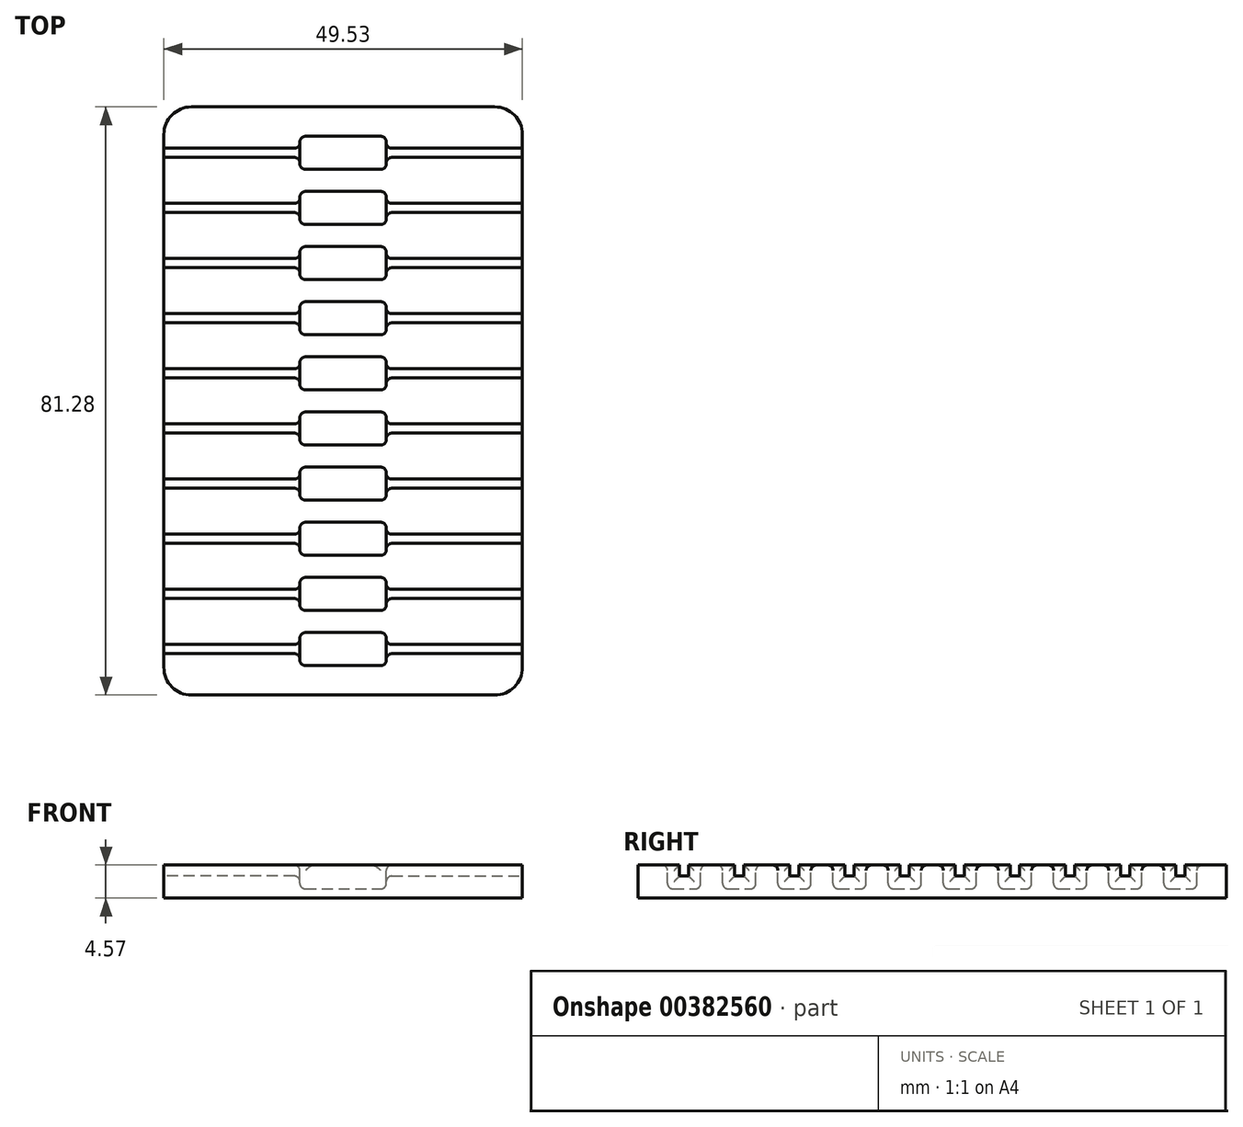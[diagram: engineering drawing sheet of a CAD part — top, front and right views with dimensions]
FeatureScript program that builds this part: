
annotation { "Feature Type Name" : "Feature", "Feature Type Description" : "" }
export const myFeature = defineFeature(function(context is Context, id is Id, definition is map)
    precondition{}
    {
        {
            var Q0;
            Q0=qCreatedBy(makeId("Top.planeOp"),FACE);
            var sketch = newSketch(context, id + "F0", { "sketchPlane" : qUnion([Q0])});
            skLineSegment(sketch, "E0.bottom", {"start": v(0, 0) * mm, "end": v(49.53, 0) * mm});
            skLineSegment(sketch, "E0.top", {"start": v(0, 81.28) * mm, "end": v(49.53, 81.28) * mm});
            skLineSegment(sketch, "E0.left", {"start": v(0, 0) * mm, "end": v(0, 81.28) * mm});
            skLineSegment(sketch, "E0.right", {"start": v(49.53, 0) * mm, "end": v(49.53, 81.28) * mm});
            skSolve(sketch);
        }
        {
            var Q0;
            Q0=qSketchRegion(id+"F0",true);
            extrude(context, id + "F1", {"entities" : qUnion([Q0]), "depth" : 4.57 * mm});
        }
        {
            var Q0;
            Q0=makeQuery(id+"F1.opExtrude","CAP_FACE",FACE,{"disambiguationData":[OSD([sQuery(id+"F0.wireOp",EDGE,"E0.bottom"),sQuery(id+"F0.wireOp",EDGE,"E0.top"),sQuery(id+"F0.wireOp",EDGE,"E0.left"),sQuery(id+"F0.wireOp",EDGE,"E0.right")])],"isStart":false});
            var sketch = newSketch(context, id + "F2", { "sketchPlane" : qUnion([Q0])});
            skLineSegment(sketch, "E1.bottom", {"start": v(18.8, 4.06) * mm, "end": v(30.73, 4.06) * mm});
            skLineSegment(sketch, "E1.top", {"start": v(18.8, 8.64) * mm, "end": v(30.73, 8.64) * mm});
            skLineSegment(sketch, "E1.left", {"start": v(18.8, 4.06) * mm, "end": v(18.8, 8.64) * mm});
            skLineSegment(sketch, "E1.right", {"start": v(30.73, 4.06) * mm, "end": v(30.73, 8.64) * mm});
            skLineSegment(sketch, "E2", {"start": v(30.73, 6.35) * mm, "end": v(49.53, 6.35) * mm, "construction": true});
            skLineSegment(sketch, "E3.0.1.0", {"start": v(18.8, 16.26) * mm, "end": v(30.73, 16.26) * mm});
            skLineSegment(sketch, "E3.0.1.1", {"start": v(18.8, 11.68) * mm, "end": v(30.73, 11.68) * mm});
            skLineSegment(sketch, "E3.0.1.2", {"start": v(30.73, 11.68) * mm, "end": v(30.73, 16.26) * mm});
            skLineSegment(sketch, "E3.0.1.3", {"start": v(18.8, 11.68) * mm, "end": v(18.8, 16.26) * mm});
            skLineSegment(sketch, "E3.0.2.0", {"start": v(18.8, 23.88) * mm, "end": v(30.73, 23.88) * mm});
            skLineSegment(sketch, "E3.0.2.1", {"start": v(18.8, 19.3) * mm, "end": v(30.73, 19.3) * mm});
            skLineSegment(sketch, "E3.0.2.2", {"start": v(30.73, 19.3) * mm, "end": v(30.73, 23.88) * mm});
            skLineSegment(sketch, "E3.0.2.3", {"start": v(18.8, 19.3) * mm, "end": v(18.8, 23.88) * mm});
            skLineSegment(sketch, "E3.0.3.0", {"start": v(18.8, 31.5) * mm, "end": v(30.73, 31.5) * mm});
            skLineSegment(sketch, "E3.0.3.1", {"start": v(18.8, 26.92) * mm, "end": v(30.73, 26.92) * mm});
            skLineSegment(sketch, "E3.0.3.2", {"start": v(30.73, 26.92) * mm, "end": v(30.73, 31.5) * mm});
            skLineSegment(sketch, "E3.0.3.3", {"start": v(18.8, 26.92) * mm, "end": v(18.8, 31.5) * mm});
            skLineSegment(sketch, "E3.0.4.0", {"start": v(18.8, 39.12) * mm, "end": v(30.73, 39.12) * mm});
            skLineSegment(sketch, "E3.0.4.1", {"start": v(18.8, 34.54) * mm, "end": v(30.73, 34.54) * mm});
            skLineSegment(sketch, "E3.0.4.2", {"start": v(30.73, 34.54) * mm, "end": v(30.73, 39.12) * mm});
            skLineSegment(sketch, "E3.0.4.3", {"start": v(18.8, 34.54) * mm, "end": v(18.8, 39.12) * mm});
            skLineSegment(sketch, "E3.0.5.0", {"start": v(18.8, 46.74) * mm, "end": v(30.73, 46.74) * mm});
            skLineSegment(sketch, "E3.0.5.1", {"start": v(18.8, 42.16) * mm, "end": v(30.73, 42.16) * mm});
            skLineSegment(sketch, "E3.0.5.2", {"start": v(30.73, 42.16) * mm, "end": v(30.73, 46.74) * mm});
            skLineSegment(sketch, "E3.0.5.3", {"start": v(18.8, 42.16) * mm, "end": v(18.8, 46.74) * mm});
            skLineSegment(sketch, "E3.0.6.0", {"start": v(18.8, 54.36) * mm, "end": v(30.73, 54.36) * mm});
            skLineSegment(sketch, "E3.0.6.1", {"start": v(18.8, 49.78) * mm, "end": v(30.73, 49.78) * mm});
            skLineSegment(sketch, "E3.0.6.2", {"start": v(30.73, 49.78) * mm, "end": v(30.73, 54.36) * mm});
            skLineSegment(sketch, "E3.0.6.3", {"start": v(18.8, 49.78) * mm, "end": v(18.8, 54.36) * mm});
            skLineSegment(sketch, "E3.0.7.0", {"start": v(18.8, 61.98) * mm, "end": v(30.73, 61.98) * mm});
            skLineSegment(sketch, "E3.0.7.1", {"start": v(18.8, 57.4) * mm, "end": v(30.73, 57.4) * mm});
            skLineSegment(sketch, "E3.0.7.2", {"start": v(30.73, 57.4) * mm, "end": v(30.73, 61.98) * mm});
            skLineSegment(sketch, "E3.0.7.3", {"start": v(18.8, 57.4) * mm, "end": v(18.8, 61.98) * mm});
            skLineSegment(sketch, "E3.0.8.0", {"start": v(18.8, 69.6) * mm, "end": v(30.73, 69.6) * mm});
            skLineSegment(sketch, "E3.0.8.1", {"start": v(18.8, 65.02) * mm, "end": v(30.73, 65.02) * mm});
            skLineSegment(sketch, "E3.0.8.2", {"start": v(30.73, 65.02) * mm, "end": v(30.73, 69.6) * mm});
            skLineSegment(sketch, "E3.0.8.3", {"start": v(18.8, 65.02) * mm, "end": v(18.8, 69.6) * mm});
            skLineSegment(sketch, "E3.0.9.0", {"start": v(18.8, 77.22) * mm, "end": v(30.73, 77.22) * mm});
            skLineSegment(sketch, "E3.0.9.1", {"start": v(18.8, 72.64) * mm, "end": v(30.73, 72.64) * mm});
            skLineSegment(sketch, "E3.0.9.2", {"start": v(30.73, 72.64) * mm, "end": v(30.73, 77.22) * mm});
            skLineSegment(sketch, "E3.0.9.3", {"start": v(18.8, 72.64) * mm, "end": v(18.8, 77.22) * mm});
            skLineSegment(sketch, "E3.direction1", {"start": v(18.8, 4.06) * mm, "end": v(44.2, 4.06) * mm, "construction": true});
            skLineSegment(sketch, "E3.direction2", {"start": v(18.8, 4.06) * mm, "end": v(18.8, 11.68) * mm, "construction": true});
            skSolve(sketch);
        }
        {
            var Q0;
            Q0=qSketchRegion(id+"F2",true);
            extrude(context, id + "F3", {"entities" : qUnion([Q0]), "operationType" : NewBodyOperationType.REMOVE, "oppositeDirection" : true, "depth" : 3.3 * mm});
        }
        {
            var Q0;
            Q0=makeQuery(id+"F1.opExtrude","CAP_FACE",FACE,{"disambiguationData":[OSD([sQuery(id+"F0.wireOp",EDGE,"E0.bottom"),sQuery(id+"F0.wireOp",EDGE,"E0.top"),sQuery(id+"F0.wireOp",EDGE,"E0.left"),sQuery(id+"F0.wireOp",EDGE,"E0.right")])],"isStart":false});
            var sketch = newSketch(context, id + "F4", { "sketchPlane" : qUnion([Q0])});
            skLineSegment(sketch, "E4.bottom", {"start": v(30.73, 5.72) * mm, "end": v(49.53, 5.72) * mm});
            skLineSegment(sketch, "E4.top", {"start": v(30.73, 6.99) * mm, "end": v(49.53, 6.99) * mm});
            skLineSegment(sketch, "E4.left", {"start": v(30.73, 5.72) * mm, "end": v(30.73, 6.99) * mm});
            skLineSegment(sketch, "E4.right", {"start": v(49.53, 5.72) * mm, "end": v(49.53, 6.99) * mm});
            skPoint(sketch, "E5.firstSnap0", {"position": v(40.13, 6.99) * mm});
            skLineSegment(sketch, "E5.bottom", {"start": v(18.8, 6.99) * mm, "end": v(0, 6.99) * mm});
            skLineSegment(sketch, "E5.top", {"start": v(18.8, 5.72) * mm, "end": v(0, 5.72) * mm});
            skLineSegment(sketch, "E5.left", {"start": v(18.8, 6.99) * mm, "end": v(18.8, 5.72) * mm});
            skLineSegment(sketch, "E5.right", {"start": v(0, 6.99) * mm, "end": v(0, 5.72) * mm});
            skLineSegment(sketch, "E6", {"start": v(30.73, 6.35) * mm, "end": v(49.53, 6.35) * mm, "construction": true});
            skLineSegment(sketch, "E7.0.1.0", {"start": v(18.8, 13.34) * mm, "end": v(0, 13.33) * mm});
            skLineSegment(sketch, "E7.0.1.1", {"start": v(30.73, 13.97) * mm, "end": v(49.53, 13.97) * mm, "construction": true});
            skLineSegment(sketch, "E7.0.1.2", {"start": v(18.8, 14.6) * mm, "end": v(0, 14.6) * mm});
            skLineSegment(sketch, "E7.0.1.3", {"start": v(30.73, 14.6) * mm, "end": v(49.53, 14.6) * mm});
            skLineSegment(sketch, "E7.0.1.4", {"start": v(30.73, 13.33) * mm, "end": v(49.53, 13.33) * mm});
            skPoint(sketch, "E7.0.1.5", {"position": v(40.13, 14.6) * mm});
            skLineSegment(sketch, "E7.0.1.6", {"start": v(18.8, 14.6) * mm, "end": v(18.8, 13.33) * mm});
            skLineSegment(sketch, "E7.0.1.7", {"start": v(0, 14.6) * mm, "end": v(0, 13.33) * mm});
            skLineSegment(sketch, "E7.0.1.8", {"start": v(49.53, 13.33) * mm, "end": v(49.53, 14.6) * mm});
            skLineSegment(sketch, "E7.0.1.9", {"start": v(30.73, 13.33) * mm, "end": v(30.73, 14.6) * mm});
            skLineSegment(sketch, "E7.0.2.0", {"start": v(18.8, 20.95) * mm, "end": v(0, 20.95) * mm});
            skLineSegment(sketch, "E7.0.2.1", {"start": v(30.73, 21.6) * mm, "end": v(49.53, 21.6) * mm, "construction": true});
            skLineSegment(sketch, "E7.0.2.2", {"start": v(18.8, 22.22) * mm, "end": v(0, 22.22) * mm});
            skLineSegment(sketch, "E7.0.2.3", {"start": v(30.73, 22.22) * mm, "end": v(49.53, 22.22) * mm});
            skLineSegment(sketch, "E7.0.2.4", {"start": v(30.73, 20.95) * mm, "end": v(49.53, 20.95) * mm});
            skPoint(sketch, "E7.0.2.5", {"position": v(40.13, 22.22) * mm});
            skLineSegment(sketch, "E7.0.2.6", {"start": v(18.8, 22.22) * mm, "end": v(18.8, 20.95) * mm});
            skLineSegment(sketch, "E7.0.2.7", {"start": v(0, 22.22) * mm, "end": v(0, 20.95) * mm});
            skLineSegment(sketch, "E7.0.2.8", {"start": v(49.53, 20.95) * mm, "end": v(49.53, 22.22) * mm});
            skLineSegment(sketch, "E7.0.2.9", {"start": v(30.73, 20.95) * mm, "end": v(30.73, 22.22) * mm});
            skLineSegment(sketch, "E7.0.3.0", {"start": v(18.8, 28.57) * mm, "end": v(0, 28.57) * mm});
            skLineSegment(sketch, "E7.0.3.1", {"start": v(30.73, 29.21) * mm, "end": v(49.53, 29.21) * mm, "construction": true});
            skLineSegment(sketch, "E7.0.3.2", {"start": v(18.8, 29.84) * mm, "end": v(0, 29.84) * mm});
            skLineSegment(sketch, "E7.0.3.3", {"start": v(30.73, 29.84) * mm, "end": v(49.53, 29.84) * mm});
            skLineSegment(sketch, "E7.0.3.4", {"start": v(30.73, 28.57) * mm, "end": v(49.53, 28.57) * mm});
            skPoint(sketch, "E7.0.3.5", {"position": v(40.13, 29.84) * mm});
            skLineSegment(sketch, "E7.0.3.6", {"start": v(18.8, 29.84) * mm, "end": v(18.8, 28.57) * mm});
            skLineSegment(sketch, "E7.0.3.7", {"start": v(0, 29.84) * mm, "end": v(0, 28.57) * mm});
            skLineSegment(sketch, "E7.0.3.8", {"start": v(49.53, 28.57) * mm, "end": v(49.53, 29.84) * mm});
            skLineSegment(sketch, "E7.0.3.9", {"start": v(30.73, 28.57) * mm, "end": v(30.73, 29.84) * mm});
            skLineSegment(sketch, "E7.0.4.0", {"start": v(18.8, 36.2) * mm, "end": v(0, 36.2) * mm});
            skLineSegment(sketch, "E7.0.4.1", {"start": v(30.73, 36.83) * mm, "end": v(49.53, 36.83) * mm, "construction": true});
            skLineSegment(sketch, "E7.0.4.2", {"start": v(18.8, 37.46) * mm, "end": v(0, 37.46) * mm});
            skLineSegment(sketch, "E7.0.4.3", {"start": v(30.73, 37.46) * mm, "end": v(49.53, 37.46) * mm});
            skLineSegment(sketch, "E7.0.4.4", {"start": v(30.73, 36.2) * mm, "end": v(49.53, 36.2) * mm});
            skPoint(sketch, "E7.0.4.5", {"position": v(40.13, 37.46) * mm});
            skLineSegment(sketch, "E7.0.4.6", {"start": v(18.8, 37.46) * mm, "end": v(18.8, 36.2) * mm});
            skLineSegment(sketch, "E7.0.4.7", {"start": v(0, 37.46) * mm, "end": v(0, 36.2) * mm});
            skLineSegment(sketch, "E7.0.4.8", {"start": v(49.53, 36.2) * mm, "end": v(49.53, 37.46) * mm});
            skLineSegment(sketch, "E7.0.4.9", {"start": v(30.73, 36.2) * mm, "end": v(30.73, 37.46) * mm});
            skLineSegment(sketch, "E7.0.5.0", {"start": v(18.8, 43.81) * mm, "end": v(0, 43.81) * mm});
            skLineSegment(sketch, "E7.0.5.1", {"start": v(30.73, 44.45) * mm, "end": v(49.53, 44.45) * mm, "construction": true});
            skLineSegment(sketch, "E7.0.5.2", {"start": v(18.8, 45.08) * mm, "end": v(0, 45.08) * mm});
            skLineSegment(sketch, "E7.0.5.3", {"start": v(30.73, 45.08) * mm, "end": v(49.53, 45.08) * mm});
            skLineSegment(sketch, "E7.0.5.4", {"start": v(30.73, 43.81) * mm, "end": v(49.53, 43.81) * mm});
            skPoint(sketch, "E7.0.5.5", {"position": v(40.13, 45.08) * mm});
            skLineSegment(sketch, "E7.0.5.6", {"start": v(18.8, 45.08) * mm, "end": v(18.8, 43.81) * mm});
            skLineSegment(sketch, "E7.0.5.7", {"start": v(0, 45.08) * mm, "end": v(0, 43.81) * mm});
            skLineSegment(sketch, "E7.0.5.8", {"start": v(49.53, 43.81) * mm, "end": v(49.53, 45.08) * mm});
            skLineSegment(sketch, "E7.0.5.9", {"start": v(30.73, 43.81) * mm, "end": v(30.73, 45.08) * mm});
            skLineSegment(sketch, "E7.0.6.0", {"start": v(18.8, 51.43) * mm, "end": v(0, 51.43) * mm});
            skLineSegment(sketch, "E7.0.6.1", {"start": v(30.73, 52.07) * mm, "end": v(49.53, 52.07) * mm, "construction": true});
            skLineSegment(sketch, "E7.0.6.2", {"start": v(18.8, 52.7) * mm, "end": v(0, 52.7) * mm});
            skLineSegment(sketch, "E7.0.6.3", {"start": v(30.73, 52.7) * mm, "end": v(49.53, 52.7) * mm});
            skLineSegment(sketch, "E7.0.6.4", {"start": v(30.73, 51.43) * mm, "end": v(49.53, 51.43) * mm});
            skPoint(sketch, "E7.0.6.5", {"position": v(40.13, 52.7) * mm});
            skLineSegment(sketch, "E7.0.6.6", {"start": v(18.8, 52.7) * mm, "end": v(18.8, 51.43) * mm});
            skLineSegment(sketch, "E7.0.6.7", {"start": v(0, 52.7) * mm, "end": v(0, 51.43) * mm});
            skLineSegment(sketch, "E7.0.6.8", {"start": v(49.53, 51.43) * mm, "end": v(49.53, 52.7) * mm});
            skLineSegment(sketch, "E7.0.6.9", {"start": v(30.73, 51.43) * mm, "end": v(30.73, 52.7) * mm});
            skLineSegment(sketch, "E7.0.7.0", {"start": v(18.8, 59.05) * mm, "end": v(0, 59.05) * mm});
            skLineSegment(sketch, "E7.0.7.1", {"start": v(30.73, 59.69) * mm, "end": v(49.53, 59.69) * mm, "construction": true});
            skLineSegment(sketch, "E7.0.7.2", {"start": v(18.8, 60.32) * mm, "end": v(0, 60.32) * mm});
            skLineSegment(sketch, "E7.0.7.3", {"start": v(30.73, 60.32) * mm, "end": v(49.53, 60.32) * mm});
            skLineSegment(sketch, "E7.0.7.4", {"start": v(30.73, 59.05) * mm, "end": v(49.53, 59.05) * mm});
            skPoint(sketch, "E7.0.7.5", {"position": v(40.13, 60.32) * mm});
            skLineSegment(sketch, "E7.0.7.6", {"start": v(18.8, 60.32) * mm, "end": v(18.8, 59.05) * mm});
            skLineSegment(sketch, "E7.0.7.7", {"start": v(0, 60.32) * mm, "end": v(0, 59.05) * mm});
            skLineSegment(sketch, "E7.0.7.8", {"start": v(49.53, 59.05) * mm, "end": v(49.53, 60.32) * mm});
            skLineSegment(sketch, "E7.0.7.9", {"start": v(30.73, 59.05) * mm, "end": v(30.73, 60.32) * mm});
            skLineSegment(sketch, "E7.0.8.0", {"start": v(18.8, 66.67) * mm, "end": v(0, 66.67) * mm});
            skLineSegment(sketch, "E7.0.8.1", {"start": v(30.73, 67.3) * mm, "end": v(49.53, 67.3) * mm, "construction": true});
            skLineSegment(sketch, "E7.0.8.2", {"start": v(18.8, 67.94) * mm, "end": v(0, 67.94) * mm});
            skLineSegment(sketch, "E7.0.8.3", {"start": v(30.73, 67.94) * mm, "end": v(49.53, 67.94) * mm});
            skLineSegment(sketch, "E7.0.8.4", {"start": v(30.73, 66.67) * mm, "end": v(49.53, 66.67) * mm});
            skPoint(sketch, "E7.0.8.5", {"position": v(40.13, 67.94) * mm});
            skLineSegment(sketch, "E7.0.8.6", {"start": v(18.8, 67.94) * mm, "end": v(18.8, 66.67) * mm});
            skLineSegment(sketch, "E7.0.8.7", {"start": v(0, 67.94) * mm, "end": v(0, 66.67) * mm});
            skLineSegment(sketch, "E7.0.8.8", {"start": v(49.53, 66.67) * mm, "end": v(49.53, 67.94) * mm});
            skLineSegment(sketch, "E7.0.8.9", {"start": v(30.73, 66.67) * mm, "end": v(30.73, 67.94) * mm});
            skLineSegment(sketch, "E7.0.9.0", {"start": v(18.8, 74.3) * mm, "end": v(0, 74.3) * mm});
            skLineSegment(sketch, "E7.0.9.1", {"start": v(30.73, 74.93) * mm, "end": v(49.53, 74.93) * mm, "construction": true});
            skLineSegment(sketch, "E7.0.9.2", {"start": v(18.8, 75.56) * mm, "end": v(0, 75.56) * mm});
            skLineSegment(sketch, "E7.0.9.3", {"start": v(30.73, 75.56) * mm, "end": v(49.53, 75.56) * mm});
            skLineSegment(sketch, "E7.0.9.4", {"start": v(30.73, 74.3) * mm, "end": v(49.53, 74.3) * mm});
            skPoint(sketch, "E7.0.9.5", {"position": v(40.13, 75.56) * mm});
            skLineSegment(sketch, "E7.0.9.6", {"start": v(18.8, 75.56) * mm, "end": v(18.8, 74.3) * mm});
            skLineSegment(sketch, "E7.0.9.7", {"start": v(0, 75.56) * mm, "end": v(0, 74.3) * mm});
            skLineSegment(sketch, "E7.0.9.8", {"start": v(49.53, 74.3) * mm, "end": v(49.53, 75.56) * mm});
            skLineSegment(sketch, "E7.0.9.9", {"start": v(30.73, 74.3) * mm, "end": v(30.73, 75.56) * mm});
            skLineSegment(sketch, "E7.direction1", {"start": v(0, 5.72) * mm, "end": v(25.4, 5.72) * mm, "construction": true});
            skLineSegment(sketch, "E7.direction2", {"start": v(0, 5.72) * mm, "end": v(0, 13.33) * mm, "construction": true});
            skSolve(sketch);
        }
        {
            var Q0;
            Q0=qSketchRegion(id+"F4",true);
            extrude(context, id + "F5", {"entities" : qUnion([Q0]), "operationType" : NewBodyOperationType.REMOVE, "oppositeDirection" : true, "depth" : 1.52 * mm});
        }
        {
            var Q0;
            Q0=makeQuery(id+"F3.boolean.opBoolean","COPY",FACE,{"derivedFrom":makeQuery(id+"F3.opExtrude","SWEPT_FACE",FACE,{"disambiguationData":[OSD([sQuery(id+"F2.wireOp",EDGE,"E1.bottom")])]})});
            var Q1;
            Q1=makeQuery(id+"F3.boolean.opBoolean","COPY",FACE,{"derivedFrom":makeQuery(id+"F3.opExtrude","SWEPT_FACE",FACE,{"disambiguationData":[OSD([sQuery(id+"F2.wireOp",EDGE,"E1.left")])]})});
            var Q2;
            Q2=makeQuery(id+"F3.boolean.opBoolean","COPY",FACE,{"derivedFrom":makeQuery(id+"F3.opExtrude","SWEPT_FACE",FACE,{"disambiguationData":[OSD([sQuery(id+"F2.wireOp",EDGE,"E1.right")])]})});
            var Q3;
            Q3=makeQuery(id+"F3.boolean.opBoolean","COPY",FACE,{"derivedFrom":makeQuery(id+"F3.opExtrude","SWEPT_FACE",FACE,{"disambiguationData":[OSD([sQuery(id+"F2.wireOp",EDGE,"E1.top")])]})});
            var Q4;
            Q4=makeQuery(id+"F3.boolean.opBoolean","COPY",FACE,{"derivedFrom":makeQuery(id+"F3.opExtrude","SWEPT_FACE",FACE,{"disambiguationData":[OSD([sQuery(id+"F2.wireOp",EDGE,"E3.0.1.3")])]})});
            var Q5;
            Q5=makeQuery(id+"F3.boolean.opBoolean","COPY",FACE,{"derivedFrom":makeQuery(id+"F3.opExtrude","SWEPT_FACE",FACE,{"disambiguationData":[OSD([sQuery(id+"F2.wireOp",EDGE,"E3.0.2.3")])]})});
            var Q6;
            Q6=makeQuery(id+"F3.boolean.opBoolean","COPY",FACE,{"derivedFrom":makeQuery(id+"F3.opExtrude","SWEPT_FACE",FACE,{"disambiguationData":[OSD([sQuery(id+"F2.wireOp",EDGE,"E3.0.3.3")])]})});
            var Q7;
            Q7=makeQuery(id+"F3.boolean.opBoolean","COPY",FACE,{"derivedFrom":makeQuery(id+"F3.opExtrude","SWEPT_FACE",FACE,{"disambiguationData":[OSD([sQuery(id+"F2.wireOp",EDGE,"E3.0.4.3")])]})});
            var Q8;
            Q8=makeQuery(id+"F3.boolean.opBoolean","COPY",FACE,{"derivedFrom":makeQuery(id+"F3.opExtrude","SWEPT_FACE",FACE,{"disambiguationData":[OSD([sQuery(id+"F2.wireOp",EDGE,"E3.0.5.3")])]})});
            var Q9;
            Q9=makeQuery(id+"F3.boolean.opBoolean","COPY",FACE,{"derivedFrom":makeQuery(id+"F3.opExtrude","SWEPT_FACE",FACE,{"disambiguationData":[OSD([sQuery(id+"F2.wireOp",EDGE,"E3.0.6.3")])]})});
            var Q10;
            Q10=makeQuery(id+"F3.boolean.opBoolean","COPY",FACE,{"derivedFrom":makeQuery(id+"F3.opExtrude","SWEPT_FACE",FACE,{"disambiguationData":[OSD([sQuery(id+"F2.wireOp",EDGE,"E3.0.7.3")])]})});
            var Q11;
            Q11=makeQuery(id+"F3.boolean.opBoolean","COPY",FACE,{"derivedFrom":makeQuery(id+"F3.opExtrude","SWEPT_FACE",FACE,{"disambiguationData":[OSD([sQuery(id+"F2.wireOp",EDGE,"E3.0.8.3")])]})});
            var Q12;
            Q12=makeQuery(id+"F3.boolean.opBoolean","COPY",FACE,{"derivedFrom":makeQuery(id+"F3.opExtrude","SWEPT_FACE",FACE,{"disambiguationData":[OSD([sQuery(id+"F2.wireOp",EDGE,"E3.0.9.3")])]})});
            var Q13;
            Q13=makeQuery(id+"F3.boolean.opBoolean","COPY",FACE,{"derivedFrom":makeQuery(id+"F3.opExtrude","SWEPT_FACE",FACE,{"disambiguationData":[OSD([sQuery(id+"F2.wireOp",EDGE,"E3.0.9.2")])]})});
            var Q14;
            Q14=makeQuery(id+"F3.boolean.opBoolean","COPY",FACE,{"derivedFrom":makeQuery(id+"F3.opExtrude","SWEPT_FACE",FACE,{"disambiguationData":[OSD([sQuery(id+"F2.wireOp",EDGE,"E3.0.8.2")])]})});
            var Q15;
            Q15=makeQuery(id+"F3.boolean.opBoolean","COPY",FACE,{"derivedFrom":makeQuery(id+"F3.opExtrude","SWEPT_FACE",FACE,{"disambiguationData":[OSD([sQuery(id+"F2.wireOp",EDGE,"E3.0.7.2")])]})});
            var Q16;
            Q16=makeQuery(id+"F3.boolean.opBoolean","COPY",FACE,{"derivedFrom":makeQuery(id+"F3.opExtrude","SWEPT_FACE",FACE,{"disambiguationData":[OSD([sQuery(id+"F2.wireOp",EDGE,"E3.0.6.2")])]})});
            var Q17;
            Q17=makeQuery(id+"F3.boolean.opBoolean","COPY",FACE,{"derivedFrom":makeQuery(id+"F3.opExtrude","SWEPT_FACE",FACE,{"disambiguationData":[OSD([sQuery(id+"F2.wireOp",EDGE,"E3.0.5.2")])]})});
            var Q18;
            Q18=makeQuery(id+"F3.boolean.opBoolean","COPY",FACE,{"derivedFrom":makeQuery(id+"F3.opExtrude","SWEPT_FACE",FACE,{"disambiguationData":[OSD([sQuery(id+"F2.wireOp",EDGE,"E3.0.4.2")])]})});
            var Q19;
            Q19=makeQuery(id+"F3.boolean.opBoolean","COPY",FACE,{"derivedFrom":makeQuery(id+"F3.opExtrude","SWEPT_FACE",FACE,{"disambiguationData":[OSD([sQuery(id+"F2.wireOp",EDGE,"E3.0.3.2")])]})});
            var Q20;
            Q20=makeQuery(id+"F3.boolean.opBoolean","COPY",FACE,{"derivedFrom":makeQuery(id+"F3.opExtrude","SWEPT_FACE",FACE,{"disambiguationData":[OSD([sQuery(id+"F2.wireOp",EDGE,"E3.0.2.2")])]})});
            var Q21;
            Q21=makeQuery(id+"F3.boolean.opBoolean","COPY",FACE,{"derivedFrom":makeQuery(id+"F3.opExtrude","SWEPT_FACE",FACE,{"disambiguationData":[OSD([sQuery(id+"F2.wireOp",EDGE,"E3.0.1.2")])]})});
            var Q22;
            Q22=makeQuery(id+"F3.boolean.opBoolean","COPY",FACE,{"derivedFrom":makeQuery(id+"F3.opExtrude","SWEPT_FACE",FACE,{"disambiguationData":[OSD([sQuery(id+"F2.wireOp",EDGE,"E3.0.1.1")])]})});
            var Q23;
            Q23=makeQuery(id+"F3.boolean.opBoolean","COPY",FACE,{"derivedFrom":makeQuery(id+"F3.opExtrude","SWEPT_FACE",FACE,{"disambiguationData":[OSD([sQuery(id+"F2.wireOp",EDGE,"E3.0.1.0")])]})});
            var Q24;
            Q24=makeQuery(id+"F3.boolean.opBoolean","COPY",FACE,{"derivedFrom":makeQuery(id+"F3.opExtrude","CAP_FACE",FACE,{"disambiguationData":[OSD([sQuery(id+"F2.wireOp",EDGE,"E3.0.2.0"),sQuery(id+"F2.wireOp",EDGE,"E3.0.2.1"),sQuery(id+"F2.wireOp",EDGE,"E3.0.2.2"),sQuery(id+"F2.wireOp",EDGE,"E3.0.2.3")])],"isStart":false})});
            var Q25;
            Q25=makeQuery(id+"F3.boolean.opBoolean","COPY",FACE,{"derivedFrom":makeQuery(id+"F3.opExtrude","CAP_FACE",FACE,{"disambiguationData":[OSD([sQuery(id+"F2.wireOp",EDGE,"E3.0.3.0"),sQuery(id+"F2.wireOp",EDGE,"E3.0.3.1"),sQuery(id+"F2.wireOp",EDGE,"E3.0.3.2"),sQuery(id+"F2.wireOp",EDGE,"E3.0.3.3")])],"isStart":false})});
            var Q26;
            Q26=makeQuery(id+"F3.boolean.opBoolean","COPY",FACE,{"derivedFrom":makeQuery(id+"F3.opExtrude","CAP_FACE",FACE,{"disambiguationData":[OSD([sQuery(id+"F2.wireOp",EDGE,"E3.0.4.0"),sQuery(id+"F2.wireOp",EDGE,"E3.0.4.1"),sQuery(id+"F2.wireOp",EDGE,"E3.0.4.2"),sQuery(id+"F2.wireOp",EDGE,"E3.0.4.3")])],"isStart":false})});
            var Q27;
            Q27=makeQuery(id+"F3.boolean.opBoolean","COPY",FACE,{"derivedFrom":makeQuery(id+"F3.opExtrude","CAP_FACE",FACE,{"disambiguationData":[OSD([sQuery(id+"F2.wireOp",EDGE,"E3.0.5.0"),sQuery(id+"F2.wireOp",EDGE,"E3.0.5.1"),sQuery(id+"F2.wireOp",EDGE,"E3.0.5.2"),sQuery(id+"F2.wireOp",EDGE,"E3.0.5.3")])],"isStart":false})});
            var Q28;
            Q28=makeQuery(id+"F3.boolean.opBoolean","COPY",FACE,{"derivedFrom":makeQuery(id+"F3.opExtrude","CAP_FACE",FACE,{"disambiguationData":[OSD([sQuery(id+"F2.wireOp",EDGE,"E3.0.6.0"),sQuery(id+"F2.wireOp",EDGE,"E3.0.6.1"),sQuery(id+"F2.wireOp",EDGE,"E3.0.6.2"),sQuery(id+"F2.wireOp",EDGE,"E3.0.6.3")])],"isStart":false})});
            var Q29;
            Q29=makeQuery(id+"F3.boolean.opBoolean","COPY",FACE,{"derivedFrom":makeQuery(id+"F3.opExtrude","CAP_FACE",FACE,{"disambiguationData":[OSD([sQuery(id+"F2.wireOp",EDGE,"E3.0.7.0"),sQuery(id+"F2.wireOp",EDGE,"E3.0.7.1"),sQuery(id+"F2.wireOp",EDGE,"E3.0.7.2"),sQuery(id+"F2.wireOp",EDGE,"E3.0.7.3")])],"isStart":false})});
            var Q30;
            Q30=makeQuery(id+"F3.boolean.opBoolean","COPY",FACE,{"derivedFrom":makeQuery(id+"F3.opExtrude","CAP_FACE",FACE,{"disambiguationData":[OSD([sQuery(id+"F2.wireOp",EDGE,"E3.0.8.0"),sQuery(id+"F2.wireOp",EDGE,"E3.0.8.1"),sQuery(id+"F2.wireOp",EDGE,"E3.0.8.2"),sQuery(id+"F2.wireOp",EDGE,"E3.0.8.3")])],"isStart":false})});
            var Q31;
            Q31=makeQuery(id+"F3.boolean.opBoolean","COPY",FACE,{"derivedFrom":makeQuery(id+"F3.opExtrude","CAP_FACE",FACE,{"disambiguationData":[OSD([sQuery(id+"F2.wireOp",EDGE,"E3.0.9.0"),sQuery(id+"F2.wireOp",EDGE,"E3.0.9.1"),sQuery(id+"F2.wireOp",EDGE,"E3.0.9.2"),sQuery(id+"F2.wireOp",EDGE,"E3.0.9.3")])],"isStart":false})});
            fillet(context, id + "F6", {"entities" : qUnion([Q0, Q1, Q2, Q3, Q4, Q5, Q6, Q7, Q8, Q9, Q10, Q11, Q12, Q13, Q14, Q15, Q16, Q17, Q18, Q19, Q20, Q21, Q22, Q23, Q24, Q25, Q26, Q27, Q28, Q29, Q30, Q31]), "radius" : 0.76 * mm, "tangentPropagation" : true, "allowEdgeOverflow" : false});
        }
        {
            var Q0;
            Q0=makeQuery(id+"F1.opExtrude","SWEPT_EDGE",EDGE,{"disambiguationData":[OSD([sQuery(id+"F0.wireOp",EDGE,"E0.bottom"),sQuery(id+"F0.wireOp",EDGE,"E0.right")])]});
            var Q1;
            Q1=makeQuery(id+"F1.opExtrude","SWEPT_EDGE",EDGE,{"disambiguationData":[OSD([sQuery(id+"F0.wireOp",EDGE,"E0.bottom"),sQuery(id+"F0.wireOp",EDGE,"E0.left")])]});
            var Q2;
            Q2=makeQuery(id+"F1.opExtrude","SWEPT_EDGE",EDGE,{"disambiguationData":[OSD([sQuery(id+"F0.wireOp",EDGE,"E0.top"),sQuery(id+"F0.wireOp",EDGE,"E0.left")])]});
            var Q3;
            Q3=makeQuery(id+"F1.opExtrude","SWEPT_EDGE",EDGE,{"disambiguationData":[OSD([sQuery(id+"F0.wireOp",EDGE,"E0.top"),sQuery(id+"F0.wireOp",EDGE,"E0.right")])]});
            fillet(context, id + "F7", {"entities" : qUnion([Q0, Q1, Q2, Q3]), "radius" : 3.8 * mm, "tangentPropagation" : true, "allowEdgeOverflow" : false});
        }
    });
